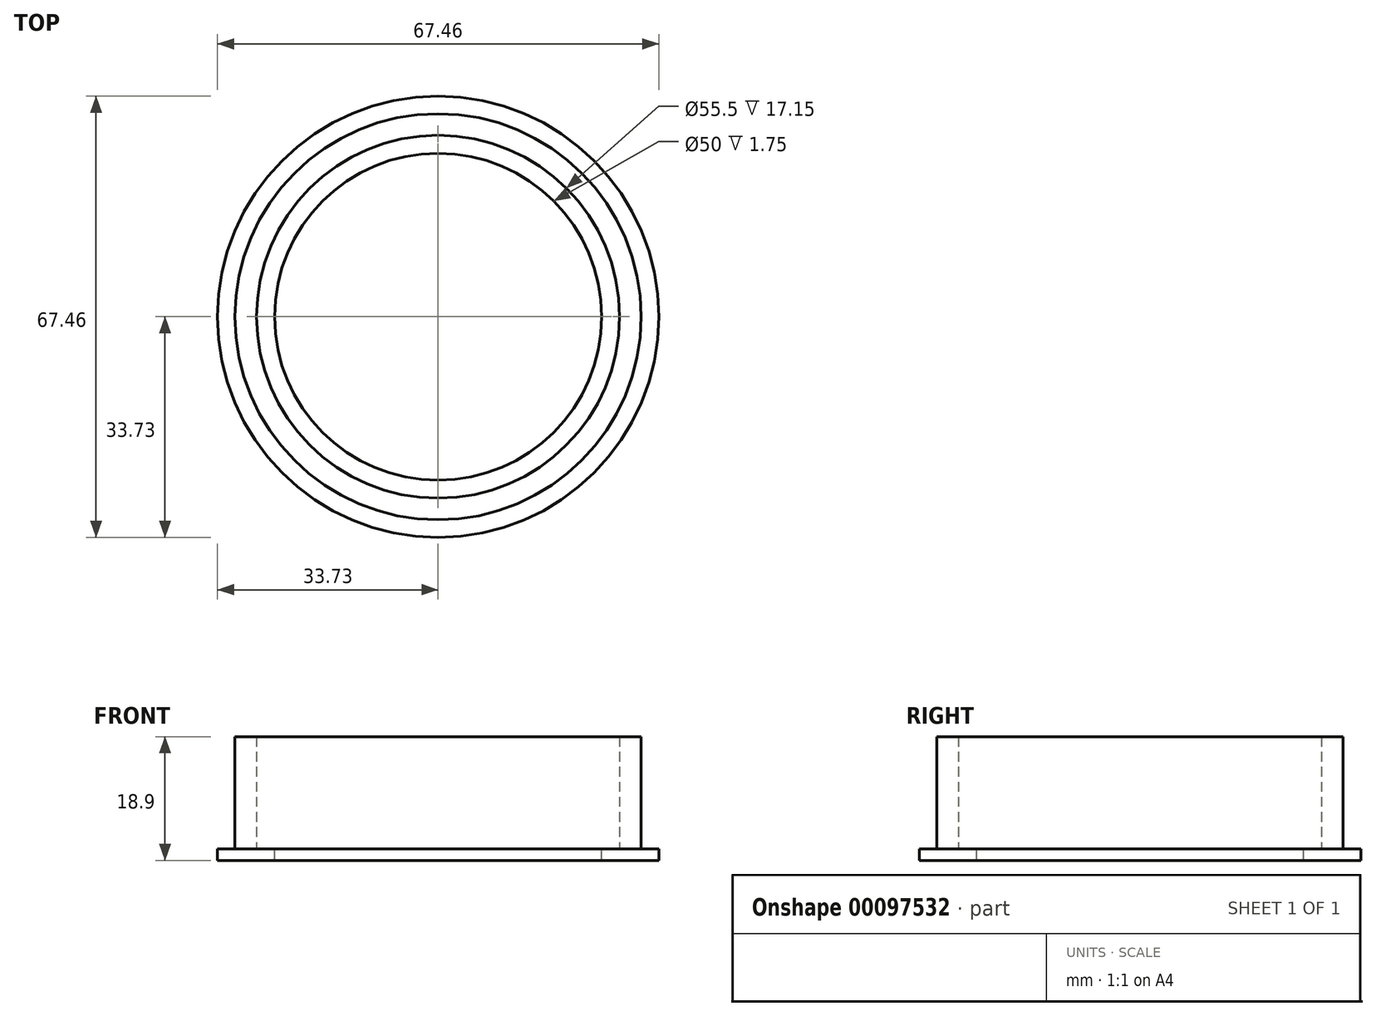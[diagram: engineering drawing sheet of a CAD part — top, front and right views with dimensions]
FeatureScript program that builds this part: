
annotation { "Feature Type Name" : "Feature", "Feature Type Description" : "" }
export const myFeature = defineFeature(function(context is Context, id is Id, definition is map)
    precondition{}
    {
        {
            var Q0;
            Q0=qCreatedBy(makeId("Top.planeOp"),FACE);
            var sketch = newSketch(context, id + "F0", { "sketchPlane" : qUnion([Q0])});
            skCircle(sketch, "E0", {"center": v(0, 0) * mm, "radius": 33.73 * mm});
            skSolve(sketch);
        }
        {
            var Q0;
            Q0=makeQuery(id+"F0.imprint","IMPRINT",FACE,{"disambiguationData":[TD([[makeQuery(id+"F0.imprint","IMPRINT",EDGE,{"derivedFrom":sQuery(id+"F0.wireOp",EDGE,"E0")}),1.0]])]});
            extrude(context, id + "F1", {"entities" : qUnion([Q0]), "depth" : 1.75 * mm});
        }
        {
            var Q0;
            Q0=makeQuery(id+"F1.opExtrude","CAP_FACE",FACE,{"disambiguationData":[OSD([sQuery(id+"F0.wireOp",EDGE,"E0")])],"isStart":false});
            var sketch = newSketch(context, id + "F2", { "sketchPlane" : qUnion([Q0])});
            skCircle(sketch, "E1", {"center": v(0, 0) * mm, "radius": 31.05 * mm});
            skCircle(sketch, "E2", {"center": v(0, 0) * mm, "radius": 27.75 * mm});
            skCircle(sketch, "E3", {"center": v(0, 0) * mm, "radius": 25 * mm});
            skSolve(sketch);
        }
        {
            var Q0;
            Q0=makeQuery(id+"F2.imprint","IMPRINT",FACE,{"disambiguationData":[TD([[makeQuery(id+"F2.imprint","IMPRINT",EDGE,{"derivedFrom":sQuery(id+"F2.wireOp",EDGE,"E1")}),1.0]])]});
            extrude(context, id + "F3", {"entities" : qUnion([Q0]), "operationType" : NewBodyOperationType.ADD, "depth" : 17.15 * mm});
        }
        {
            var Q0;
            Q0=makeQuery(id+"F2.imprint","IMPRINT",FACE,{"disambiguationData":[TD([[makeQuery(id+"F2.imprint","IMPRINT",EDGE,{"derivedFrom":sQuery(id+"F2.wireOp",EDGE,"E3")}),1.0]])]});
            extrude(context, id + "F4", {"entities" : qUnion([Q0]), "operationType" : NewBodyOperationType.REMOVE, "endBound" : BoundingType.THROUGH_ALL, "oppositeDirection" : true, "depth" : 25 * mm});
        }
    });
